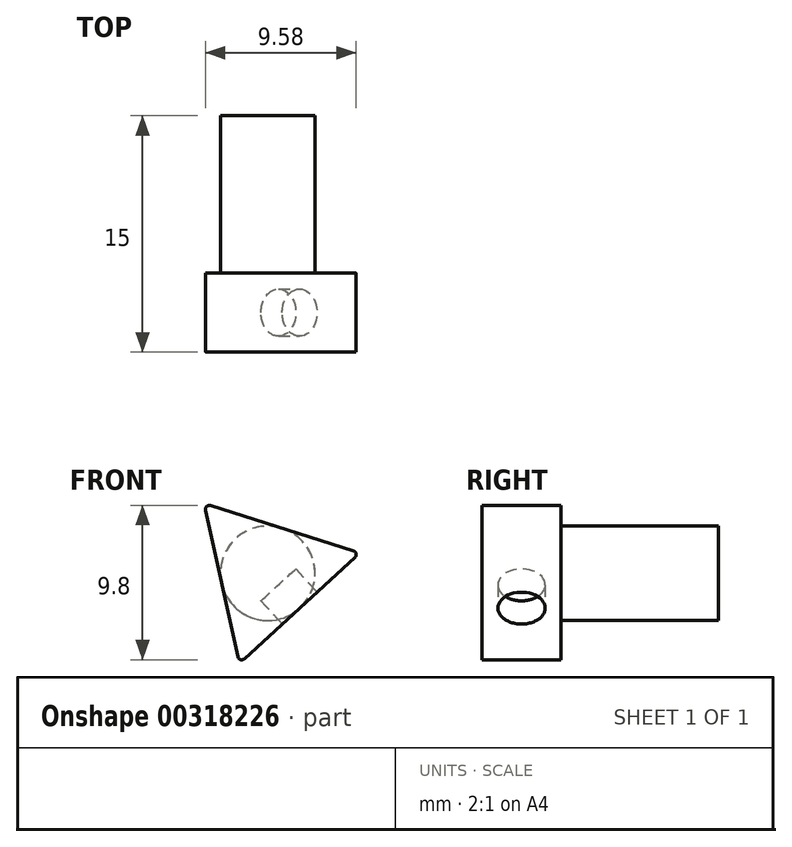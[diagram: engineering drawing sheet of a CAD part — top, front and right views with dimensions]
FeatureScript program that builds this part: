
annotation { "Feature Type Name" : "Feature", "Feature Type Description" : "" }
export const myFeature = defineFeature(function(context is Context, id is Id, definition is map)
    precondition{}
    {
        {
            var Q0;
            Q0=qCreatedBy(makeId("Front.planeOp"),FACE);
            var sketch = newSketch(context, id + "F0", { "sketchPlane" : qUnion([Q0])});
            skCircle(sketch, "E0", {"center": v(0, 0) * mm, "radius": 3 * mm});
            skSolve(sketch);
        }
        {
            var Q0;
            Q0 = qSketchRegion(id + "F0", true);
            extrude(context, id + "F1", {"entities" : qUnion([Q0]), "depth" : 10 * mm});
        }
        {
            var Q0;
            Q0=makeQuery(id+"F1.opExtrude","CAP_FACE",FACE,{"disambiguationData":[OSD([sQuery(id+"F0.wireOp",EDGE,"E0")])],"isStart":false});
            var sketch = newSketch(context, id + "F2", { "sketchPlane" : qUnion([Q0])});
            skCircle(sketch, "E1.cCircle", {"center": v(0, 0) * mm, "radius": 3 * mm, "construction": true});
            skLineSegment(sketch, "E1.0", {"start": v(-4.05, 4.43) * mm, "end": v(5.86, 1.3) * mm});
            skLineSegment(sketch, "E1.1", {"start": v(5.86, 1.3) * mm, "end": v(-1.8, -5.72) * mm});
            skLineSegment(sketch, "E1.2", {"start": v(-1.8, -5.72) * mm, "end": v(-4.05, 4.43) * mm});
            skPoint(sketch, "E1.0.midPoint", {"position": v(0.9, 2.86) * mm});
            skSolve(sketch);
        }
        {
            var Q0;
            Q0 = qSketchRegion(id + "F2", true);
            extrude(context, id + "F3", {"entities" : qUnion([Q0]), "operationType" : NewBodyOperationType.ADD, "depth" : 5 * mm});
        }
        {
            var Q0;
            Q0=qCreatedBy(makeId("Right.planeOp"),FACE);
            var sketch = newSketch(context, id + "F4", { "sketchPlane" : qUnion([Q0])});
            skLineSegment(sketch, "E2", {"start": v(46.02, 0) * mm, "end": v(-79.09, 0) * mm, "construction": true});
            skSolve(sketch);
        }
        {
            var Q0;
            Q0=makeQuery(id+"F3.opExtrude","SWEPT_FACE",FACE,{"disambiguationData":[OSD([sQuery(id+"F2.wireOp",EDGE,"E1.1")])]});
            var sketch = newSketch(context, id + "F5", { "sketchPlane" : qUnion([Q0])});
            skCircle(sketch, "E3", {"center": v(0, 12.5) * mm, "radius": 1.5 * mm});
            skSolve(sketch);
        }
        {
            var Q0;
            Q0 = qSketchRegion(id + "F5", true);
            extrude(context, id + "F6", {"entities" : qUnion([Q0]), "operationType" : NewBodyOperationType.REMOVE, "oppositeDirection" : true, "depth" : 2 * mm});
        }
        {
            var Q0;
            Q0=makeQuery(id+"F3.opExtrude","SWEPT_EDGE",EDGE,{"disambiguationData":[OSD([sQuery(id+"F2.wireOp",EDGE,"E1.0"),sQuery(id+"F2.wireOp",EDGE,"E1.1")])]});
            var Q1;
            Q1=makeQuery(id+"F3.opExtrude","SWEPT_EDGE",EDGE,{"disambiguationData":[OSD([sQuery(id+"F2.wireOp",EDGE,"E1.0"),sQuery(id+"F2.wireOp",EDGE,"E1.2")])]});
            var Q2;
            Q2=makeQuery(id+"F3.opExtrude","SWEPT_EDGE",EDGE,{"disambiguationData":[OSD([sQuery(id+"F2.wireOp",EDGE,"E1.1"),sQuery(id+"F2.wireOp",EDGE,"E1.2")])]});
            fillet(context, id + "F7", {"entities" : qUnion([Q0, Q1, Q2]), "radius" : .25 * mm, "tangentPropagation" : true, "allowEdgeOverflow" : false});
        }
    });
